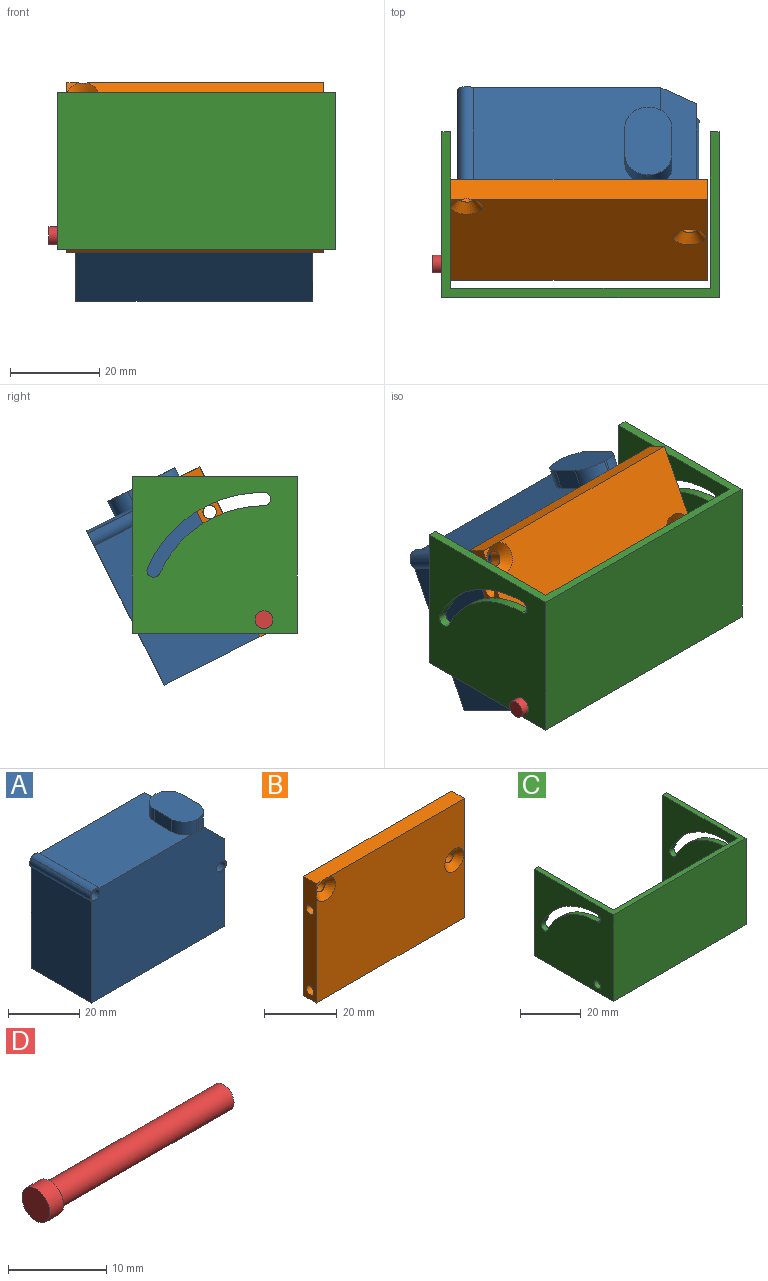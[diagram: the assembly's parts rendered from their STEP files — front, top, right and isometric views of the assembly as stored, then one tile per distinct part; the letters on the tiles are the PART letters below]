
ASSEMBLY  parts=4 mates=3
PART A: 24 faces, bbox 54.2x24x42.3 mm
  f0: plane 2.57x0.71mm, normal (0,0,1), area 0.6mm2, adj f9,f19,f23
  f1: plane 41.88x24mm, normal (0,0,1), area 880.2mm2, adj f2,f9,f10,f15,f16,f20,f21,f22
  f2: plane 54.22x38.61mm, normal (0,1,0), area 1967.4mm2, adj f1,f3,f4,f5,f6,f7,f8,f10
  f3: plane 24x7.18mm, normal (1,0,0), area 172.2mm2, adj f2,f9,f13,f23
  f4: plane 24x0.08mm, normal (-1,0,0), area 1.8mm2, adj f2,f8,f9,f12
  f5: plane 34.88x24mm, normal (-1,0,0), area 837mm2, adj f2,f6,f9,f12
  f6: plane 53x24mm, normal (0,0,-1), area 1272mm2, adj f2,f5,f7,f9
  f7: plane 24x19.78mm, normal (1,0,0), area 474.6mm2, adj f2,f6,f9,f13
  f8: plane 24x0.08mm, normal (0,0,1), area 1.8mm2, adj f2,f4,f9,f10
  f9: plane 54.22x42.33mm, normal (0,-1,0), area 1969.6mm2, adj f0,f1,f3,f4,f5,f6,f7,f8
  f10: cylinder r=2.21mm len=24mm, axis (0,-1,0), area 80.8mm2, adj f1,f2,f8,f9
  f11: cylinder r=1.72mm len=24mm, axis (0,-1,0), area 260.1mm2, adj f2,f9
  f12: cylinder r=2.21mm len=24mm, axis (0,-1,0), area 80.8mm2, adj f2,f4,f5,f9
  f13: cylinder r=2.21mm len=24mm, axis (0,-1,0), area 80.8mm2, adj f2,f3,f7,f9
  f14: cylinder r=1.7mm len=24mm, axis (0,-1,0), area 256.4mm2, adj f2,f9
  f15: plane 4.33x0.5mm, normal (0,1,0), area 2.2mm2, adj f1,f18,f20,f21
  f16: plane 6.86x4.33mm, normal (-1,0,0), area 29.7mm2, adj f1,f18,f21,f22
  f17: plane 6.86x6.76mm, normal (1,0,0), area 46.4mm2, adj f18,f19,f20,f23
  f18: plane 16.86x10.5mm, normal (0,0,1), area 155.6mm2, adj f9,f15,f16,f17,f19,f20,f21,f22
  f19: cylinder r=5mm len=6.76mm, axis (0,0,-1), area 42.2mm2, adj f0,f9,f17,f18,f23
  f20: cylinder r=5mm len=6.76mm, axis (0,0,-1), area 42.2mm2, adj f1,f15,f17,f18,f23
  f21: cylinder r=5mm len=5mm, axis (0,0,1), area 34mm2, adj f1,f15,f16,f18
  f22: cylinder r=5mm len=5mm, axis (0,0,1), area 34mm2, adj f1,f9,f16,f18
  f23: plane 24x8mm, normal (0.71,0,0.71), area 227.1mm2, adj f0,f1,f2,f3,f9,f17,f19,f20
PART B: 13 faces, bbox 57.5x5x40.1 mm
  f0: plane 57.36x40mm, normal (0,-1,0), area 2206mm2, adj f1,f2,f3,f4,f11,f12
  f1: plane 40x5mm, normal (1,0,0), area 185.9mm2, adj f0,f2,f4,f8,f9,f10
  f2: plane 57.36x5mm, normal (0,0,1), area 286.7mm2, adj f0,f1,f3,f7,f8,f12
  f3: plane 40x5mm, normal (-1,0,0), area 185.7mm2, adj f0,f2,f4,f7,f8,f9,f10,f12
  f4: plane 57.36x5mm, normal (0,0,-1), area 286.8mm2, adj f0,f1,f3,f8
  f5: cylinder r=1.7mm len=3.4mm, axis (0,1,0), area 32mm2, adj f8,f11
  f6: cylinder r=1.72mm len=3.45mm, axis (0,1,0), area 32.5mm2, adj f8,f12
  f7: plane 2.64x2.64mm, normal (0,-1,0), area 2.2mm2, adj f2,f3,f12
  f8: plane 57.36x40mm, normal (0,1,0), area 2276.1mm2, adj f1,f2,f3,f4,f5,f6
  f9: cylinder r=1.5mm len=57.36mm, axis (-1,0,0), area 540.6mm2, adj f1,f3
  f10: cylinder r=1.5mm len=57.36mm, axis (-1,0,0), area 540.6mm2, adj f1,f3
  f11: cone r=1.7mm half-angle=45deg, axis (0,-1,0), area 48mm2, adj f0,f5
  f12: cone r=1.72mm half-angle=45deg, axis (0,-1,0), area 48mm2, adj f0,f2,f3,f6,f7
PART C: 20 faces, bbox 62x37x35 mm
  f0: plane 35x35mm, normal (1,0,0), area 1117.6mm2, adj f1,f2,f3,f4,f5,f6,f8,f17
  f1: cylinder r=28.5mm len=26.03mm, axis (1,0,0), area 65.6mm2, adj f0,f2,f6,f9
  f2: cylinder r=1.5mm len=3mm, axis (1,0,0), area 9.4mm2, adj f0,f1,f3,f9
  f3: cylinder r=25.5mm len=23.29mm, axis (1,0,0), area 58.7mm2, adj f0,f2,f6,f9
  f4: plane 62x37mm, normal (0,0,1), area 264mm2, adj f0,f7,f9,f10,f16,f17,f18,f19
  f5: plane 62x37mm, normal (0,0,-1), area 264mm2, adj f0,f7,f9,f10,f16,f17,f18,f19
  f6: cylinder r=1.5mm len=2.87mm, axis (1,0,0), area 9.4mm2, adj f0,f1,f3,f9
  f7: plane 62x35mm, normal (0,-1,0), area 2170mm2, adj f4,f5,f9,f16
  f8: cylinder r=1.5mm len=3mm, axis (1,0,0), area 18.8mm2, adj f0,f9
  f9: plane 37x35mm, normal (-1,0,0), area 1187.6mm2, adj f1,f2,f3,f4,f5,f6,f7,f8
  f10: plane 35x35mm, normal (-1,0,0), area 1117.6mm2, adj f4,f5,f11,f12,f13,f14,f15,f17
  f11: cylinder r=28.5mm len=26.03mm, axis (1,0,0), area 65.6mm2, adj f10,f12,f14,f16
  f12: cylinder r=1.5mm len=3mm, axis (1,0,0), area 9.4mm2, adj f10,f11,f13,f16
  f13: cylinder r=25.5mm len=23.29mm, axis (1,0,0), area 58.7mm2, adj f10,f12,f14,f16
  f14: cylinder r=1.5mm len=2.87mm, axis (1,0,0), area 9.4mm2, adj f10,f11,f13,f16
  f15: cylinder r=1.5mm len=3mm, axis (1,0,0), area 18.8mm2, adj f10,f16
  f16: plane 37x35mm, normal (1,0,0), area 1187.6mm2, adj f4,f5,f7,f11,f12,f13,f14,f15
  f17: plane 58x35mm, normal (0,1,0), area 2030mm2, adj f0,f4,f5,f10
  f18: plane 35x2mm, normal (0,1,0), area 70mm2, adj f0,f4,f5,f9
  f19: plane 35x2mm, normal (0,1,0), area 70mm2, adj f4,f5,f10,f16
PART D: 5 faces, bbox 27x4x4 mm
  f0: cylinder r=1.5mm len=25mm, axis (1,0,0), area 235.6mm2, adj f1,f3
  f1: plane 3x3mm, normal (1,0,0), area 7.1mm2, adj f0
  f2: cylinder r=2mm len=4mm, axis (1,0,0), area 25.1mm2, adj f3,f4
  f3: plane 4x4mm, normal (1,0,0), area 5.5mm2, adj f0,f2
  f4: plane 4x4mm, normal (-1,0,0), area 12.6mm2, adj f2
PLACE A rot(axis=(-1,0,0),26.7deg) t=(22.97,32.12,-7.03)mm
PLACE B rot(axis=(-1,0,0),26.7deg) t=(22.97,32.12,-7.03)mm
PLACE C t=(22.97,34,5.11)mm
PLACE D t=(23.97,34,-21.89)mm
MATE fastened B.f6 <-> A.f10  axis (0,0.89,-0.45) through (5.6,24.75,31.71)mm
MATE revolute D.f0 <-> B.f10  axis (1,0,0) through (0,7.5,3)mm
MATE revolute C.f1 <-> B.f10  axis (-1,0,0) through (0,7.5,3)mm
